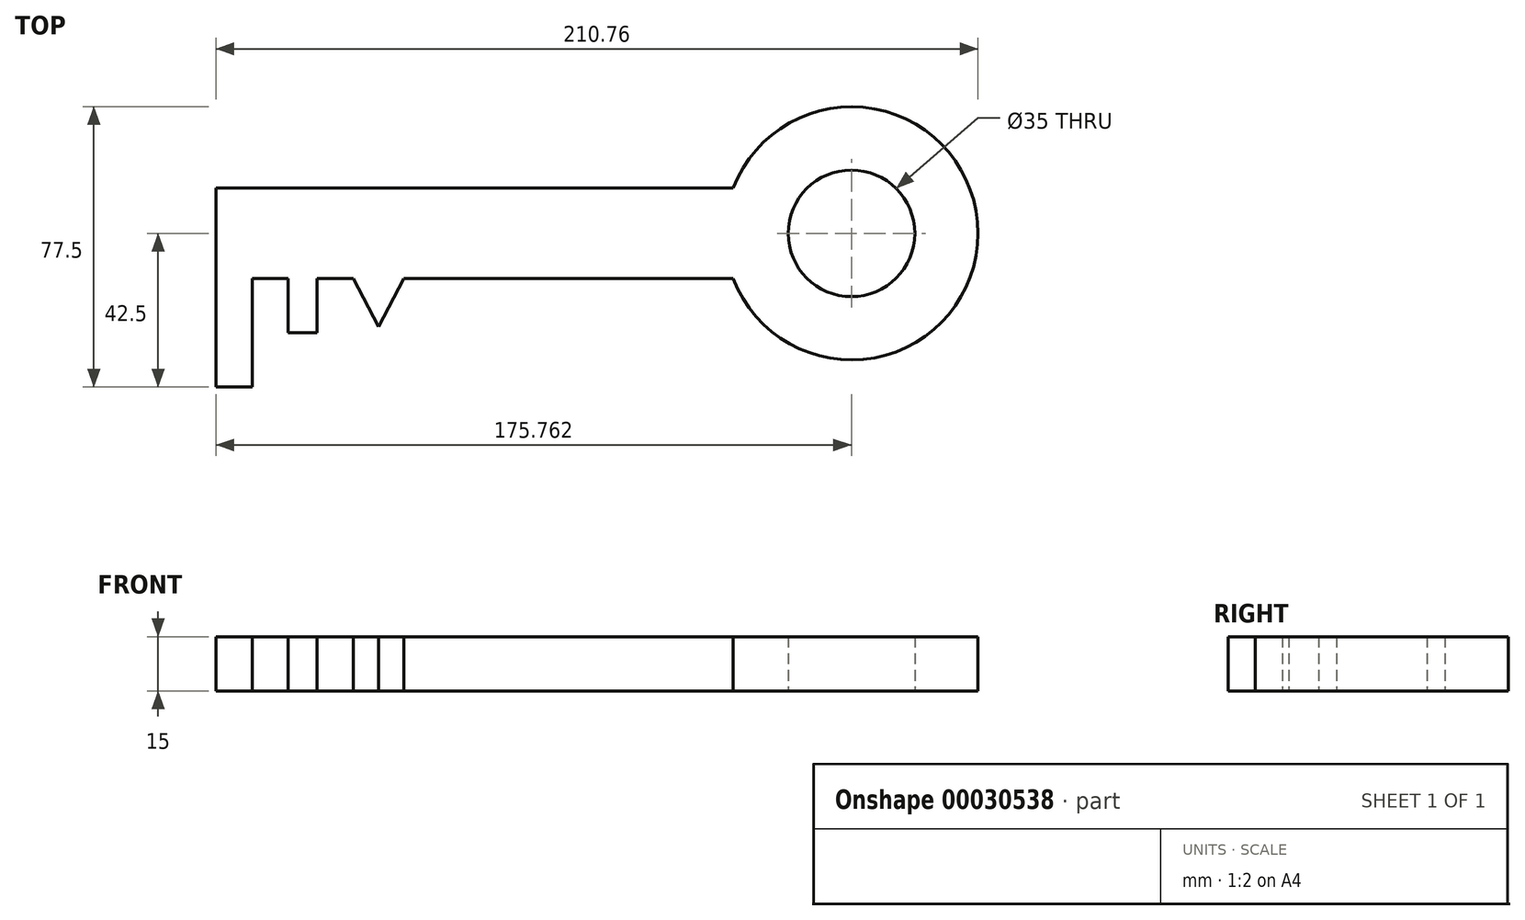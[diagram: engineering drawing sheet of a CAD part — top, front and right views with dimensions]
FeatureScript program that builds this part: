
annotation { "Feature Type Name" : "Feature", "Feature Type Description" : "" }
export const myFeature = defineFeature(function(context is Context, id is Id, definition is map)
    precondition{}
    {
        {
            var Q0;
            Q0=qCreatedBy(makeId("Top.planeOp"),FACE);
            var sketch = newSketch(context, id + "F0", { "sketchPlane" : qUnion([Q0])});
            skLineSegment(sketch, "E0.bottom", {"start": v(0, 0) * mm, "end": v(-91.07, 0) * mm});
            skLineSegment(sketch, "E0.top", {"start": v(0, 25) * mm, "end": v(-143.07, 25) * mm});
            skLineSegment(sketch, "E0.right", {"start": v(-143.07, 0) * mm, "end": v(-143.07, 25) * mm});
            skLineSegment(sketch, "E1.top", {"start": v(-143.07, -30) * mm, "end": v(-133.07, -30) * mm});
            skLineSegment(sketch, "E1.left", {"start": v(-143.07, 0) * mm, "end": v(-143.07, -30) * mm});
            skLineSegment(sketch, "E1.right", {"start": v(-133.07, 0) * mm, "end": v(-133.07, -30) * mm});
            skLineSegment(sketch, "E2.top", {"start": v(-123.07, -15) * mm, "end": v(-115.07, -15) * mm});
            skLineSegment(sketch, "E2.left", {"start": v(-123.07, 0) * mm, "end": v(-123.07, -15) * mm});
            skLineSegment(sketch, "E2.right", {"start": v(-115.07, 0) * mm, "end": v(-115.07, -15) * mm});
            skLineSegment(sketch, "E3", {"start": v(-105.07, 0) * mm, "end": v(-98.07, -13.27) * mm});
            skLineSegment(sketch, "E4", {"start": v(-91.07, 0) * mm, "end": v(-98.07, -13.27) * mm});
            skArc(sketch, "E5", {"start": v(0, 0) * mm, "mid": v(67.7, 12.5) * mm, "end": v(0, 25) * mm});
            skCircle(sketch, "E6", {"center": v(32.7, 12.5) * mm, "radius": 17.5 * mm});
            skLineSegment(sketch, "E7", {"start": v(-143.07, 12.5) * mm, "end": v(32.7, 12.5) * mm, "construction": true});
            skLineSegment(sketch, "E8.trimOffspring", {"start": v(-105.07, 0) * mm, "end": v(-115.07, 0) * mm});
            skLineSegment(sketch, "E9", {"start": v(-133.07, 0) * mm, "end": v(-123.07, 0) * mm});
            skSolve(sketch);
        }
        {
            var Q0;
            Q0=makeQuery(id+"F0.imprint","IMPRINT",FACE,{"disambiguationData":[TD([[makeQuery(id+"F0.imprint","IMPRINT",EDGE,{"derivedFrom":sQuery(id+"F0.wireOp",EDGE,"E0.bottom")}),-1.0]])]});
            extrude(context, id + "F1", {"entities" : qUnion([Q0]), "depth" : 15 * mm});
        }
    });
